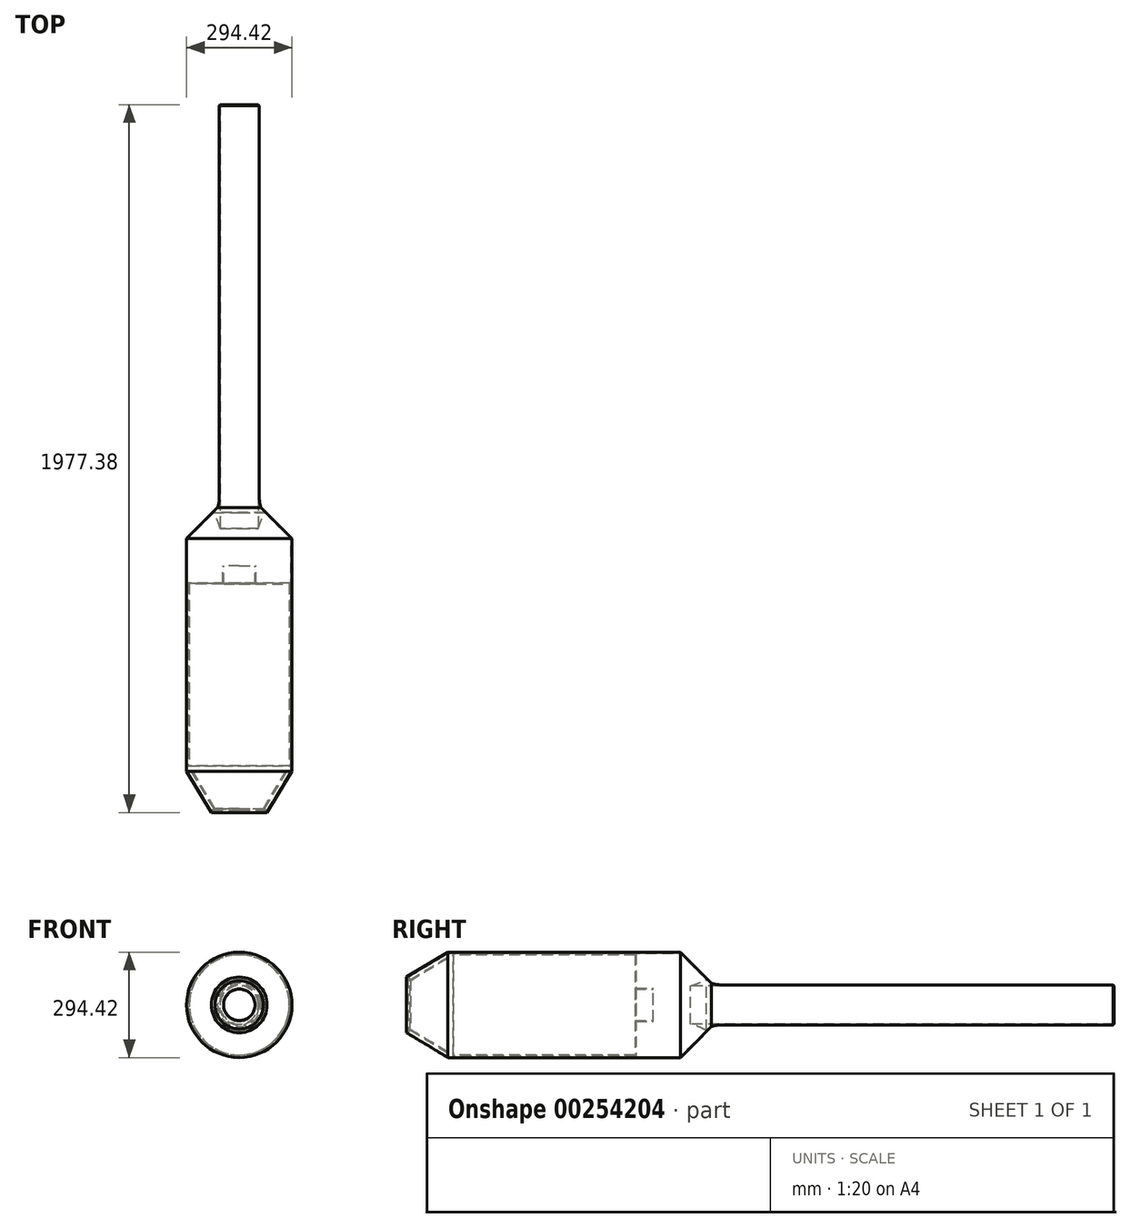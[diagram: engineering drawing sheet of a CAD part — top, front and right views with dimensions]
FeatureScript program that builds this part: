
annotation { "Feature Type Name" : "Feature", "Feature Type Description" : "" }
export const myFeature = defineFeature(function(context is Context, id is Id, definition is map)
    precondition{}
    {
        {
            var Q0;
            Q0=qCreatedBy(makeId("Front.planeOp"),FACE);
            var sketch = newSketch(context, id + "F0", { "sketchPlane" : qUnion([Q0])});
            skCircle(sketch, "E0", {"center": v(0, 0) * mm, "radius": 147.2 * mm});
            skCircle(sketch, "E1", {"center": v(0, 0) * mm, "radius": 63.5 * mm});
            skSolve(sketch);
        }
        {
            var Q0;
            Q0 = qSketchRegion(id + "F0", true);
            extrude(context, id + "F1", {"entities" : qUnion([Q0]), "depth" : 55.63 * mm});
        }
        {
            var Q0;
            Q0=makeQuery(id+"F1.opExtrude","CAP_FACE",FACE,{"disambiguationData":[OSD([sQuery(id+"F0.wireOp",EDGE,"E0"),sQuery(id+"F0.wireOp",EDGE,"E1")])],"isStart":false});
            extrude(context, id + "F2", {"entities" : qUnion([Q0]), "operationType" : NewBodyOperationType.ADD, "depth" : 86.36 * mm});
        }
        {
            var Q0;
            Q0=makeQuery(id+"F1.opExtrude","CAP_EDGE",EDGE,{"disambiguationData":[OSD([sQuery(id+"F0.wireOp",EDGE,"E0")])],"isStart":false});
            var Q1;
            Q1=makeQuery(id+"F2.opExtrude","CAP_EDGE",EDGE,{"disambiguationData":[OSD([sQuery(id+"F0.wireOp",EDGE,"E0")])],"isStart":false});
            var Q2;
            Q2=makeQuery(id+"F1.opExtrude","CAP_EDGE",EDGE,{"disambiguationData":[OSD([sQuery(id+"F0.wireOp",EDGE,"E1")])],"isStart":true});
            chamfer(context, id + "F3", {"entities" : qUnion([Q0, Q1, Q2]), "chamferType" : ChamferType.TWO_OFFSETS, "width1" : 76.2 * mm, "oppositeDirection" : false, "width2" : 127 * mm, "tangentPropagation" : true});
        }
        {
            var Q0;
            Q0=makeQuery(id+"F2.opExtrude","CAP_EDGE",EDGE,{"disambiguationData":[OSD([sQuery(id+"F0.wireOp",EDGE,"E1")])],"isStart":false});
            chamfer(context, id + "F4", {"entities" : qUnion([Q0]), "width" : 25.4 * mm, "tangentPropagation" : true});
        }
        {
            var Q0;
            Q0=makeQuery(id+"F1.opExtrude","CAP_FACE",FACE,{"disambiguationData":[OSD([sQuery(id+"F0.wireOp",EDGE,"E0"),sQuery(id+"F0.wireOp",EDGE,"E1")])],"isStart":true});
            extrude(context, id + "F5", {"entities" : qUnion([Q0]), "operationType" : NewBodyOperationType.ADD, "depth" : 711.2 * mm});
        }
        {
            var Q0;
            Q0=makeQuery(id+"F5.opExtrude","CAP_FACE",FACE,{"disambiguationData":[OSD([sQuery(id+"F0.wireOp",EDGE,"E0"),sQuery(id+"F0.wireOp",EDGE,"E1")])],"isStart":false});
            var sketch = newSketch(context, id + "F6", { "sketchPlane" : qUnion([Q0])});
            skCircle(sketch, "E2", {"center": v(0, 0) * mm, "radius": 147.01 * mm});
            skCircle(sketch, "E3", {"center": v(0, 0) * mm, "radius": 43.81 * mm});
            skSolve(sketch);
        }
        {
            var Q0;
            Q0 = qSketchRegion(id + "F6", true);
            extrude(context, id + "F7", {"entities" : qUnion([Q0]), "operationType" : NewBodyOperationType.ADD, "oppositeDirection" : true, "depth" : 203.2 * mm});
        }
        {
            var Q0;
            Q0=makeQuery(id+"F5.opExtrude","CAP_EDGE",EDGE,{"disambiguationData":[OSD([sQuery(id+"F0.wireOp",EDGE,"E0")])],"isStart":false});
            chamfer(context, id + "F8", {"entities" : qUnion([Q0]), "width" : 76.2 * mm, "tangentPropagation" : true});
        }
        {
            var Q0;
            Q0=makeQuery(id+"F7.opExtrude","CAP_EDGE",EDGE,{"disambiguationData":[OSD([sQuery(id+"F6.wireOp",EDGE,"E3")])],"isStart":true});
            fillet(context, id + "F9", {"entities" : qUnion([Q0]), "radius" : 202.36 * mm, "tangentPropagation" : true, "allowEdgeOverflow" : false});
        }
        {
            var Q0;
            Q0=qCreatedBy(makeId("Front.planeOp"),FACE);
            var sketch = newSketch(context, id + "F10", { "sketchPlane" : qUnion([Q0])});
            skCircle(sketch, "E4", {"center": v(0, 0) * mm, "radius": 56.03 * mm});
            skSolve(sketch);
        }
        {
            var Q0;
            Q0 = qSketchRegion(id + "F10", true);
            extrude(context, id + "F11", {"entities" : qUnion([Q0]), "operationType" : NewBodyOperationType.ADD, "oppositeDirection" : true, "depth" : 1854.2 * mm, "hasSecondDirection" : true, "secondDirectionOppositeDirection" : true, "secondDirectionDepth" : 581.66 * mm});
        }
        {
            var Q0;
            Q0=makeQuery(id+"F11.opExtrude","CAP_FACE",FACE,{"disambiguationData":[OSD([sQuery(id+"F10.wireOp",EDGE,"E4")])],"isStart":false});
            shell(context, id + "F12", {"entities" : qUnion([Q0]), "thickness" : 2.54 * mm});
        }
        {
            var Q0;
            {var subQ0=sQuery(id+"F10.wireOp",EDGE,"E4");Q0=makeQuery(id+"F12.opShell","OFFSET_FACE",FACE,{"disambiguationData":[OSD([subQ0]),TDD([makeQuery(id+"F11.opExtrude","CAP_FACE",FACE,{"disambiguationData":[OSD([subQ0])],"isStart":true})])]});}
            extrude(context, id + "F13", {"entities" : qUnion([Q0]), "operationType" : NewBodyOperationType.REMOVE, "oppositeDirection" : true, "depth" : 25.4 * mm});
        }
        {
            var Q0;
            Q0=makeQuery(id+"F11.opExtrude","SWEPT_FACE",FACE,{"disambiguationData":[OSD([sQuery(id+"F10.wireOp",EDGE,"E4")])]});
            chamfer(context, id + "F14", {"entities" : qUnion([Q0]), "width" : 10.16 * mm, "tangentPropagation" : true});
        }
        {
            var Q0;
            {var subQ0=makeQuery(id+"F11.opExtrude","SWEPT_FACE",FACE,{"disambiguationData":[OSD([sQuery(id+"F10.wireOp",EDGE,"E4")])]});Q0=makeQuery(id+"F14.opChamfer","BLEND_EDGE",EDGE,{"blendedFrom":[makeQuery(id+"F11.boolean.opBoolean","INTERSECT",EDGE,{"derivedFrom":[makeQuery(id+"F9.opFillet","BLEND_FACE",FACE,{"disambiguationData":[OSD([sQuery(id+"F6.wireOp",EDGE,"E3")])]}),subQ0]}),subQ0],"blendedInto":[subQ0]});}
            fillet(context, id + "F15", {"entities" : qUnion([Q0]), "radius" : 76.7 * mm, "tangentPropagation" : true, "allowEdgeOverflow" : false});
        }
    });
